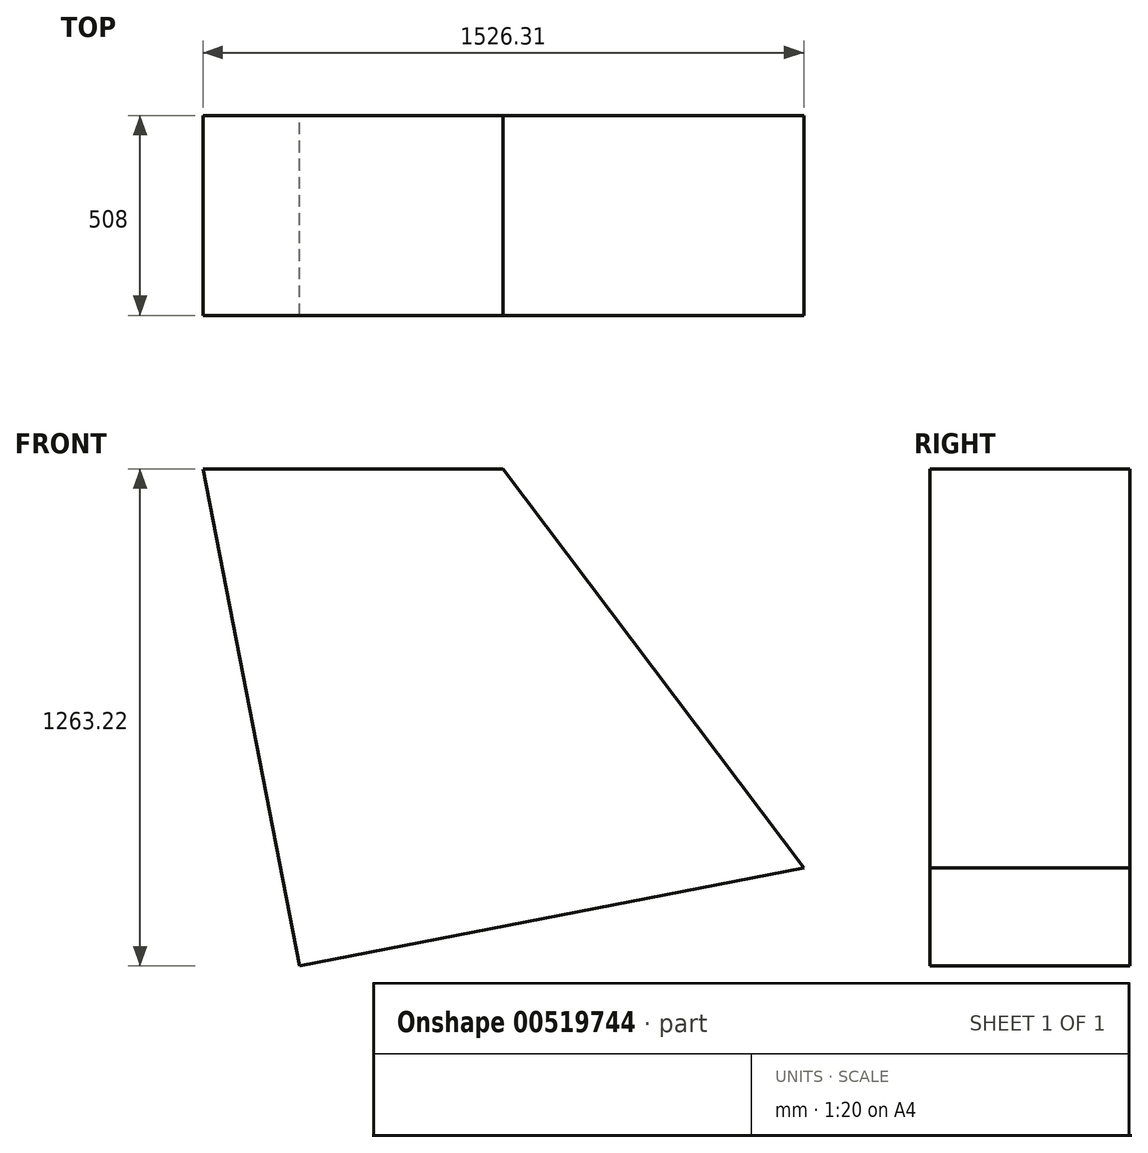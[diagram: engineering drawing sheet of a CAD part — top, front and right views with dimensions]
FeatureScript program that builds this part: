
annotation { "Feature Type Name" : "Feature", "Feature Type Description" : "" }
export const myFeature = defineFeature(function(context is Context, id is Id, definition is map)
    precondition{}
    {
        {
            var Q0;
            Q0=qCreatedBy(makeId("Front.planeOp"),FACE);
            var sketch = newSketch(context, id + "F0", { "sketchPlane" : qUnion([Q0])});
            skLineSegment(sketch, "E0", {"start": v(0, 0) * mm, "end": v(762, 0) * mm});
            skLineSegment(sketch, "E1", {"start": v(762, 0) * mm, "end": v(1526.3, -1014.27) * mm});
            skLineSegment(sketch, "E2", {"start": v(1526.3, -1014.27) * mm, "end": v(245.55, -1263.22) * mm});
            skLineSegment(sketch, "E3", {"start": v(245.55, -1263.22) * mm, "end": v(0, 0) * mm});
            skSolve(sketch);
        }
        {
            var Q0;
            Q0=makeQuery(id+"F0.imprint","IMPRINT",FACE,{"disambiguationData":[TD([[makeQuery(id+"F0.imprint","IMPRINT",EDGE,{"derivedFrom":sQuery(id+"F0.wireOp",EDGE,"E0")}),-1.0]])]});
            extrude(context, id + "F1", {"entities" : qUnion([Q0]), "depth" : 508 * mm, "offsetDistance" : 25.4 * mm});
        }
    });
